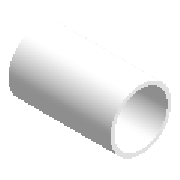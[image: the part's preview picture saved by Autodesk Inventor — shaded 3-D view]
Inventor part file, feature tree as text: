
AUTODESK INVENTOR PART (.ipt)
format: ipt  version: 2023 (Build 270158000, 158)  size: 157,696 bytes
history: native  units: mm (DEFAULTED — no unit token found)
features: other x6, revolve x1, sketch x1
ambient origin geometry x8: Origin, YZ Plane, XZ Plane, XY Plane, X Axis, Y Axis, Z Axis, Center Point
bodies: Solid1 (feature_tree)
feature tree (8):
  revolve  "Revolution1"  [1 undecoded]
  other  "Work Point1"
  other  "Work Point2"
  other  "Work Axis1"
  other  "Work Point3"
  other  "Work Axis2"
  other  "Work Point4"
  sketch  "Sketch1"  dims[d1=160.0mm d0=160.0mm d2=11.9mm d3=8.0mm d4=86.0mm d5=11.9mm d7=90.0deg]
note: 1 required parameter value undecoded (feature->parameter linkage not recoverable at this tier; creation-order binding heuristic only, values carry confidence <= 0.55)
